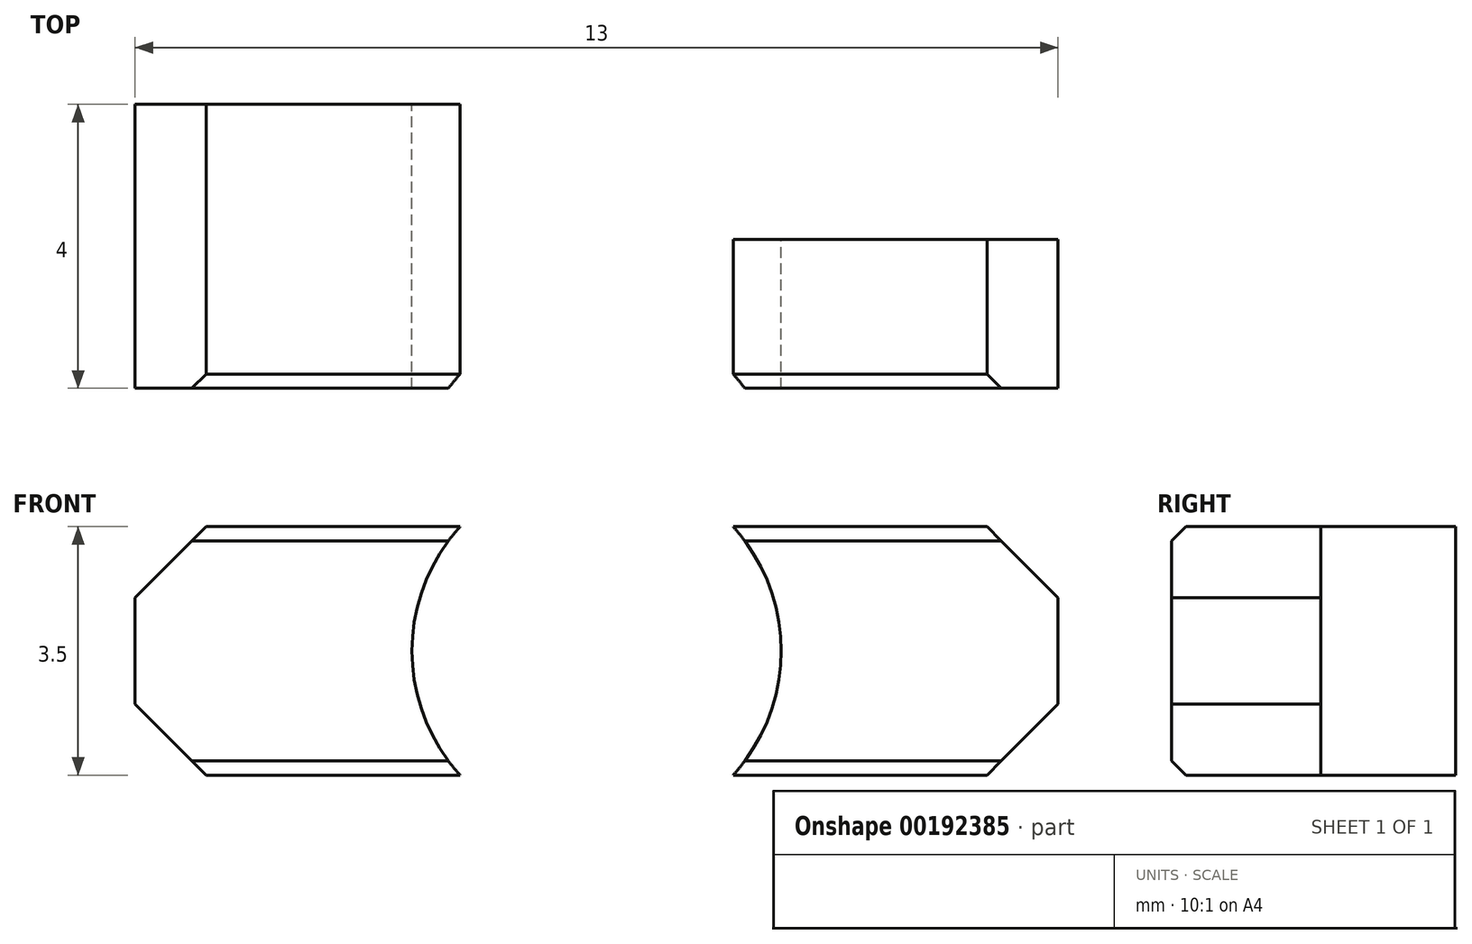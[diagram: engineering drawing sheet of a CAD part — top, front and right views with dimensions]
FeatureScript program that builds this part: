
annotation { "Feature Type Name" : "Feature", "Feature Type Description" : "" }
export const myFeature = defineFeature(function(context is Context, id is Id, definition is map)
    precondition{}
    {
        {
            var Q0;
            Q0=qCreatedBy(makeId("Front.planeOp"),FACE);
            var sketch = newSketch(context, id + "F0", { "sketchPlane" : qUnion([Q0])});
            skLineSegment(sketch, "E0.bottom", {"start": v(0, 0) * mm, "end": v(13, 0) * mm});
            skLineSegment(sketch, "E0.top", {"start": v(0, -3.5) * mm, "end": v(13, -3.5) * mm});
            skLineSegment(sketch, "E0.left", {"start": v(0, 0) * mm, "end": v(0, -3.5) * mm});
            skLineSegment(sketch, "E0.right", {"start": v(13, 0) * mm, "end": v(13, -3.5) * mm});
            skCircle(sketch, "E1", {"center": v(6.5, -1.75) * mm, "radius": 2.6 * mm});
            skPoint(sketch, "E1.centerSnap0", {"position": v(0, -1.75) * mm});
            skPoint(sketch, "E1.centerSnap1", {"position": v(6.5, -3.5) * mm});
            skSolve(sketch);
        }
        {
            var Q0;
            {var subQ0=sQuery(id+"F0.wireOp",EDGE,"E0.left");Q0=makeQuery(id+"F0.imprint","IMPRINT",FACE,{"disambiguationData":[TD([[makeQuery(id+"F0.imprint","IMPRINT",EDGE,{"derivedFrom":subQ0}),1.0]])]});}
            var Q1;
            {var subQ0=sQuery(id+"F0.wireOp",EDGE,"E1");var subQ1=sQuery(id+"F0.wireOp",EDGE,"E0.bottom");var subQ2=makeQuery(id+"F0.imprint","INTERSECT",VERTEX,{"disambiguationData":[OD(0.0)],"derivedFrom":[subQ1,subQ0]});Q1=makeQuery(id+"F0.imprint","IMPRINT",FACE,{"disambiguationData":[TD([[makeQuery(id+"F0.imprint","IMPRINT",EDGE,{"disambiguationData":[TD([[subQ2,-1.0]])],"derivedFrom":subQ1}),-1.0]])]});}
            var Q2;
            {var subQ0=sQuery(id+"F0.wireOp",EDGE,"E0.right");Q2=makeQuery(id+"F0.imprint","IMPRINT",FACE,{"disambiguationData":[TD([[makeQuery(id+"F0.imprint","IMPRINT",EDGE,{"derivedFrom":subQ0}),-1.0]])]});}
            extrude(context, id + "F1", {"entities" : qUnion([Q0, Q1, Q2]), "depth" : 4 * mm});
        }
        {
            var Q0;
            {var subQ0=sQuery(id+"F0.wireOp",EDGE,"E1");var subQ1=sQuery(id+"F0.wireOp",EDGE,"E0.bottom");var subQ2=makeQuery(id+"F0.imprint","INTERSECT",VERTEX,{"disambiguationData":[OD(0.0)],"derivedFrom":[subQ1,subQ0]});Q0=makeQuery(id+"F0.imprint","IMPRINT",FACE,{"disambiguationData":[TD([[makeQuery(id+"F0.imprint","IMPRINT",EDGE,{"disambiguationData":[TD([[subQ2,-1.0]])],"derivedFrom":subQ1}),-1.0]])]});}
            extrude(context, id + "F2", {"entities" : qUnion([Q0]), "operationType" : NewBodyOperationType.REMOVE, "depth" : 1.9 * mm});
        }
        {
            var Q0;
            Q0=makeQuery(id+"F1.opExtrude","SWEPT_EDGE",EDGE,{"disambiguationData":[OSD([sQuery(id+"F0.wireOp",EDGE,"E0.top"),sQuery(id+"F0.wireOp",EDGE,"E0.right")])]});
            var Q1;
            Q1=makeQuery(id+"F1.opExtrude","SWEPT_EDGE",EDGE,{"disambiguationData":[OSD([sQuery(id+"F0.wireOp",EDGE,"E0.bottom"),sQuery(id+"F0.wireOp",EDGE,"E0.right")])]});
            var Q2;
            Q2=makeQuery(id+"F1.opExtrude","SWEPT_EDGE",EDGE,{"disambiguationData":[OSD([sQuery(id+"F0.wireOp",EDGE,"E0.top"),sQuery(id+"F0.wireOp",EDGE,"E0.left")])]});
            var Q3;
            Q3=makeQuery(id+"F1.opExtrude","SWEPT_EDGE",EDGE,{"disambiguationData":[OSD([sQuery(id+"F0.wireOp",EDGE,"E0.bottom"),sQuery(id+"F0.wireOp",EDGE,"E0.left")])]});
            chamfer(context, id + "F3", {"entities" : qUnion([Q0, Q1, Q2, Q3]), "width" : 1 * mm, "tangentPropagation" : true});
        }
        {
            var Q0;
            Q0=makeQuery(id+"F1.opExtrude","CAP_EDGE",EDGE,{"disambiguationData":[OSD([sQuery(id+"F0.wireOp",EDGE,"E0.top")])],"isStart":false});
            var Q1;
            Q1=makeQuery(id+"F1.opExtrude","CAP_EDGE",EDGE,{"disambiguationData":[OSD([sQuery(id+"F0.wireOp",EDGE,"E0.bottom")])],"isStart":false});
            chamfer(context, id + "F4", {"entities" : qUnion([Q0, Q1]), "width" : .2 * mm, "tangentPropagation" : true});
        }
    });
